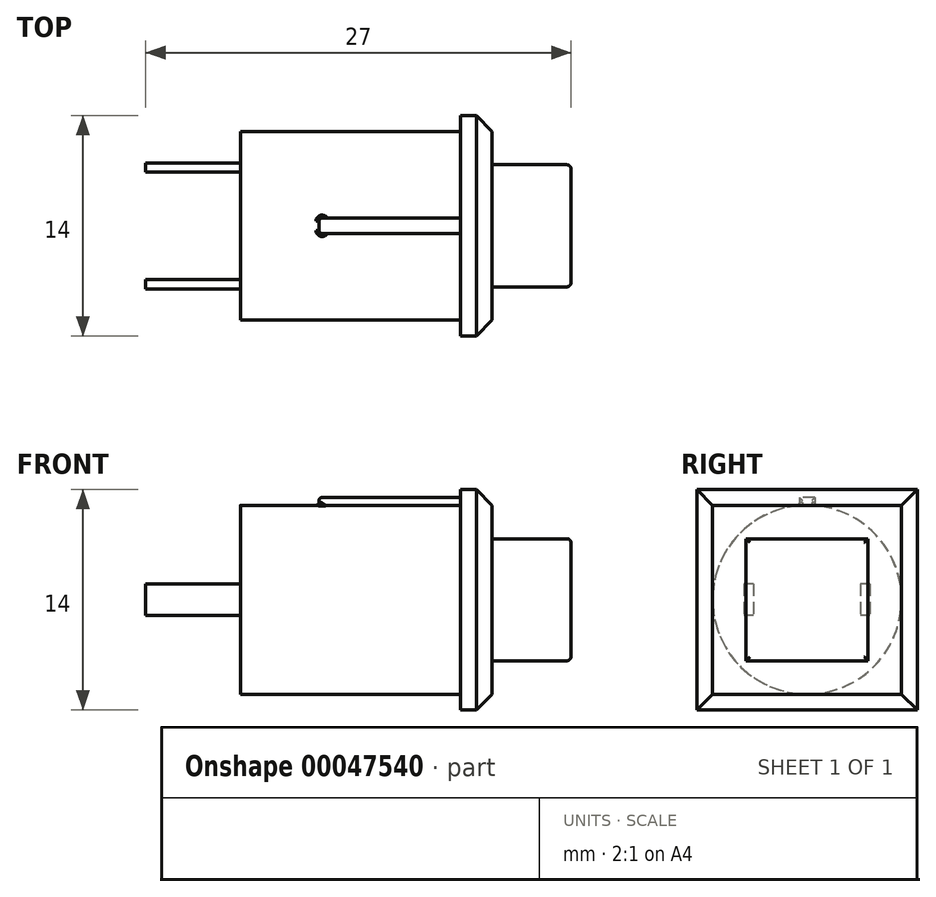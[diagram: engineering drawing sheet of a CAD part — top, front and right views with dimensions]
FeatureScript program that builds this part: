
annotation { "Feature Type Name" : "Feature", "Feature Type Description" : "" }
export const myFeature = defineFeature(function(context is Context, id is Id, definition is map)
    precondition{}
    {
        {
            var Q0;
            Q0=qCreatedBy(makeId("Right.planeOp"),FACE);
            var sketch = newSketch(context, id + "F0", { "sketchPlane" : qUnion([Q0])});
            skCircle(sketch, "E0", {"center": v(0, 0) * mm, "radius": 6 * mm});
            skSolve(sketch);
        }
        {
            var Q0;
            Q0 = qSketchRegion(id + "F0", true);
            extrude(context, id + "F1", {"entities" : qUnion([Q0]), "depth" : 14 * mm});
        }
        {
            var Q0;
            Q0=makeQuery(id+"F1.opExtrude","CAP_FACE",FACE,{"disambiguationData":[OSD([sQuery(id+"F0.wireOp",EDGE,"E0")])],"isStart":false});
            var sketch = newSketch(context, id + "F2", { "sketchPlane" : qUnion([Q0])});
            skLineSegment(sketch, "E1.bottom", {"start": v(-7, 7) * mm, "end": v(7, 7) * mm});
            skLineSegment(sketch, "E1.top", {"start": v(-7, -7) * mm, "end": v(7, -7) * mm});
            skLineSegment(sketch, "E1.left", {"start": v(-7, 7) * mm, "end": v(-7, -7) * mm});
            skLineSegment(sketch, "E1.right", {"start": v(7, 7) * mm, "end": v(7, -7) * mm});
            skSolve(sketch);
        }
        {
            var Q0;
            Q0 = qSketchRegion(id + "F2", true);
            extrude(context, id + "F3", {"entities" : qUnion([Q0]), "operationType" : NewBodyOperationType.ADD, "depth" : 2 * mm});
        }
        {
            var Q0;
            Q0=makeQuery(id+"F3.opExtrude","CAP_FACE",FACE,{"disambiguationData":[OSD([sQuery(id+"F2.wireOp",EDGE,"E1.bottom"),sQuery(id+"F2.wireOp",EDGE,"E1.top"),sQuery(id+"F2.wireOp",EDGE,"E1.left"),sQuery(id+"F2.wireOp",EDGE,"E1.right")])],"isStart":false});
            var sketch = newSketch(context, id + "F4", { "sketchPlane" : qUnion([Q0])});
            skLineSegment(sketch, "E2.bottom", {"start": v(-3.88, 3.87) * mm, "end": v(3.88, 3.87) * mm});
            skLineSegment(sketch, "E2.top", {"start": v(-3.88, -3.88) * mm, "end": v(3.88, -3.88) * mm});
            skLineSegment(sketch, "E2.left", {"start": v(-3.88, 3.87) * mm, "end": v(-3.88, -3.88) * mm});
            skLineSegment(sketch, "E2.right", {"start": v(3.88, 3.87) * mm, "end": v(3.88, -3.88) * mm});
            skSolve(sketch);
        }
        {
            var Q0;
            Q0 = qSketchRegion(id + "F4", true);
            extrude(context, id + "F5", {"entities" : qUnion([Q0]), "operationType" : NewBodyOperationType.ADD, "depth" : 5 * mm});
        }
        {
            var Q0;
            Q0=makeQuery(id+"F1.opExtrude","CAP_FACE",FACE,{"disambiguationData":[OSD([sQuery(id+"F0.wireOp",EDGE,"E0")])],"isStart":true});
            var sketch = newSketch(context, id + "F6", { "sketchPlane" : qUnion([Q0])});
            skLineSegment(sketch, "E3.bottom", {"start": v(-4, 1) * mm, "end": v(-3.4, 1) * mm});
            skLineSegment(sketch, "E3.top", {"start": v(-4, -1) * mm, "end": v(-3.4, -1) * mm});
            skLineSegment(sketch, "E3.left", {"start": v(-4, 1) * mm, "end": v(-4, -1) * mm});
            skLineSegment(sketch, "E3.right", {"start": v(-3.4, 1) * mm, "end": v(-3.4, -1) * mm});
            skLineSegment(sketch, "E4.bottom", {"start": v(3.4, 1) * mm, "end": v(4, 1) * mm});
            skLineSegment(sketch, "E4.top", {"start": v(3.4, -1) * mm, "end": v(4, -1) * mm});
            skLineSegment(sketch, "E4.left", {"start": v(3.4, 1) * mm, "end": v(3.4, -1) * mm});
            skLineSegment(sketch, "E4.right", {"start": v(4, 1) * mm, "end": v(4, -1) * mm});
            skSolve(sketch);
        }
        {
            var Q0;
            Q0 = qSketchRegion(id + "F6", true);
            extrude(context, id + "F7", {"entities" : qUnion([Q0]), "operationType" : NewBodyOperationType.ADD, "depth" : 6 * mm});
        }
        {
            var Q0;
            Q0=makeQuery(id+"F5.opExtrude","CAP_FACE",FACE,{"disambiguationData":[OSD([sQuery(id+"F4.wireOp",EDGE,"E2.bottom"),sQuery(id+"F4.wireOp",EDGE,"E2.top"),sQuery(id+"F4.wireOp",EDGE,"E2.left"),sQuery(id+"F4.wireOp",EDGE,"E2.right")])],"isStart":false});
            fillet(context, id + "F8", {"entities" : qUnion([Q0]), "radius" : .25 * mm, "tangentPropagation" : true, "allowEdgeOverflow" : false});
        }
        {
            var Q0;
            Q0=makeQuery(id+"F3.opExtrude","CAP_EDGE",EDGE,{"disambiguationData":[OSD([sQuery(id+"F2.wireOp",EDGE,"E1.top")])],"isStart":false});
            var Q1;
            Q1=makeQuery(id+"F3.opExtrude","CAP_EDGE",EDGE,{"disambiguationData":[OSD([sQuery(id+"F2.wireOp",EDGE,"E1.left")])],"isStart":false});
            var Q2;
            Q2=makeQuery(id+"F3.opExtrude","CAP_EDGE",EDGE,{"disambiguationData":[OSD([sQuery(id+"F2.wireOp",EDGE,"E1.bottom")])],"isStart":false});
            var Q3;
            Q3=makeQuery(id+"F3.opExtrude","CAP_EDGE",EDGE,{"disambiguationData":[OSD([sQuery(id+"F2.wireOp",EDGE,"E1.right")])],"isStart":false});
            chamfer(context, id + "F9", {"entities" : qUnion([Q0, Q1, Q2, Q3]), "width" : 1 * mm, "tangentPropagation" : true});
        }
        {
            var Q0;
            Q0=makeQuery(id+"F3.opExtrude","CAP_FACE",FACE,{"disambiguationData":[OSD([sQuery(id+"F2.wireOp",EDGE,"E1.bottom"),sQuery(id+"F2.wireOp",EDGE,"E1.top"),sQuery(id+"F2.wireOp",EDGE,"E1.left"),sQuery(id+"F2.wireOp",EDGE,"E1.right")])],"isStart":true});
            var sketch = newSketch(context, id + "F10", { "sketchPlane" : qUnion([Q0])});
            skLineSegment(sketch, "E5", {"start": v(-0.5, 6.5) * mm, "end": v(-0.5, 6) * mm});
            skLineSegment(sketch, "E6", {"start": v(0.5, 6.5) * mm, "end": v(0.5, 6) * mm});
            skLineSegment(sketch, "E7", {"start": v(-0.5, 6.5) * mm, "end": v(0.5, 6.5) * mm});
            skLineSegment(sketch, "E8", {"start": v(-0.5, 5.9) * mm, "end": v(0.5, 5.9) * mm});
            skLineSegment(sketch, "E9", {"start": v(0.5, 6) * mm, "end": v(0.5, 5.9) * mm});
            skLineSegment(sketch, "E10", {"start": v(-0.5, 6) * mm, "end": v(-0.5, 5.9) * mm});
            skPoint(sketch, "E11.start.orphan", {"position": v(0, 6) * mm});
            skSolve(sketch);
        }
        {
            var Q0;
            Q0 = qSketchRegion(id + "F10", true);
            extrude(context, id + "F11", {"entities" : qUnion([Q0]), "operationType" : NewBodyOperationType.ADD, "depth" : 9 * mm});
        }
        {
            var Q0;
            Q0=makeQuery(id+"F11.opExtrude","CAP_FACE",FACE,{"disambiguationData":[OSD([sQuery(id+"F10.wireOp",EDGE,"E5"),sQuery(id+"F10.wireOp",EDGE,"E6"),sQuery(id+"F10.wireOp",EDGE,"E7"),sQuery(id+"F10.wireOp",EDGE,"E8"),sQuery(id+"F10.wireOp",EDGE,"E9"),sQuery(id+"F10.wireOp",EDGE,"E10")])],"isStart":false});
            fillet(context, id + "F12", {"entities" : qUnion([Q0]), "radius" : .2 * mm, "tangentPropagation" : true, "allowEdgeOverflow" : false});
        }
    });
